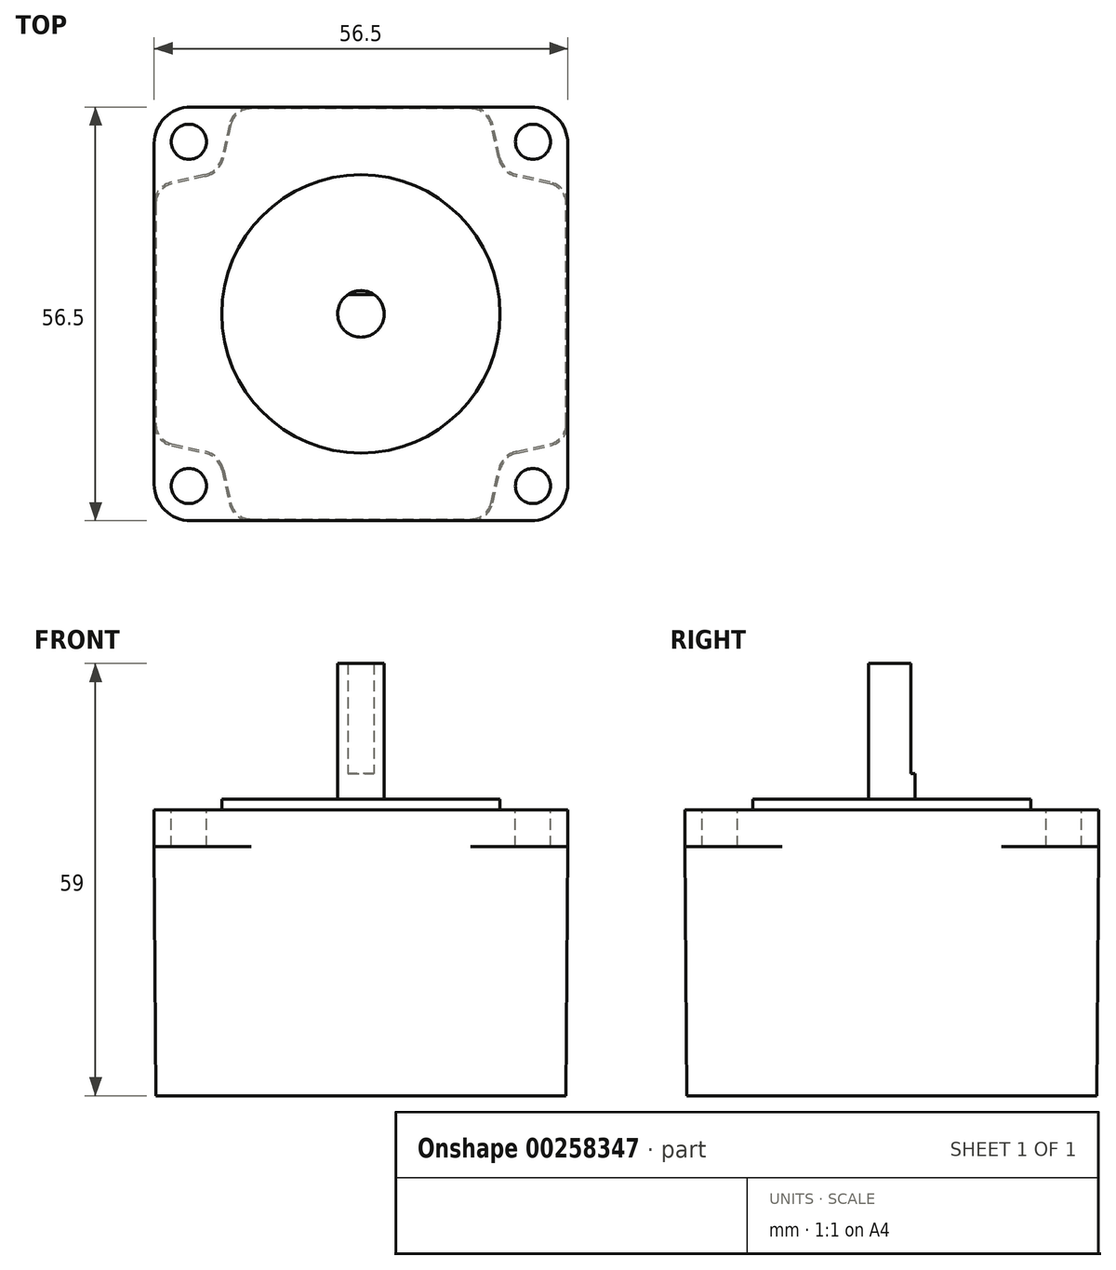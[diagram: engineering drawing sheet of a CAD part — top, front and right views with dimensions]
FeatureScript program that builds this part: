
annotation { "Feature Type Name" : "Feature", "Feature Type Description" : "" }
export const myFeature = defineFeature(function(context is Context, id is Id, definition is map)
    precondition{}
    {
        {
            var Q0;
            Q0=qCreatedBy(makeId("Top.planeOp"),FACE);
            var sketch = newSketch(context, id + "F0", { "sketchPlane" : qUnion([Q0])});
            skLineSegment(sketch, "E0.bottom", {"start": v(28.25, -28.25) * mm, "end": v(-28.25, -28.25) * mm});
            skLineSegment(sketch, "E0.top", {"start": v(28.25, 28.25) * mm, "end": v(-28.25, 28.25) * mm});
            skLineSegment(sketch, "E0.left", {"start": v(28.25, -28.25) * mm, "end": v(28.25, 28.25) * mm});
            skLineSegment(sketch, "E0.right", {"start": v(-28.25, -28.25) * mm, "end": v(-28.25, 28.25) * mm});
            skPoint(sketch, "E0.middle", {"position": v(0, 0) * mm});
            skSolve(sketch);
        }
        {
            var Q0;
            Q0=qSketchRegion(id+"F0",true);
            extrude(context, id + "F1", {"entities" : qUnion([Q0]), "oppositeDirection" : true, "depth" : 5 * mm});
        }
        {
            var Q0;
            Q0=makeQuery(id+"F1.opExtrude","CAP_FACE",FACE,{"disambiguationData":[OSD([sQuery(id+"F0.wireOp",EDGE,"E0.bottom"),sQuery(id+"F0.wireOp",EDGE,"E0.top"),sQuery(id+"F0.wireOp",EDGE,"E0.left"),sQuery(id+"F0.wireOp",EDGE,"E0.right")])],"isStart":false});
            var sketch = newSketch(context, id + "F2", { "sketchPlane" : qUnion([Q0])});
            skLineSegment(sketch, "E1", {"start": v(28.25, 0) * mm, "end": v(-28.25, 0) * mm, "construction": true});
            skLineSegment(sketch, "E2", {"start": v(0, 28.25) * mm, "end": v(0, -28.25) * mm, "construction": true});
            skLineSegment(sketch, "E3", {"start": v(0, 28.25) * mm, "end": v(-15, 28.25) * mm});
            skLineSegment(sketch, "E4", {"start": v(-18, 25.84) * mm, "end": v(-19, 21.33) * mm});
            skLineSegment(sketch, "E5", {"start": v(-21.33, 19) * mm, "end": v(-25.84, 18) * mm});
            skLineSegment(sketch, "E6", {"start": v(-28.25, 15) * mm, "end": v(-28.25, 0) * mm});
            skPoint(sketch, "E7.visualSharp", {"position": v(-19.42, 19.42) * mm});
            skArc(sketch, "E7.filletArc", {"start": v(-21.33, 19) * mm, "mid": v(-19.83, 19.83) * mm, "end": v(-19, 21.33) * mm});
            skPoint(sketch, "E8.visualSharp", {"position": v(-17.47, 28.25) * mm});
            skArc(sketch, "E8.filletArc", {"start": v(-15, 28.25) * mm, "mid": v(-16.92, 27.57) * mm, "end": v(-18, 25.84) * mm});
            skPoint(sketch, "E9.visualSharp", {"position": v(-28.25, 17.47) * mm});
            skArc(sketch, "E9.filletArc", {"start": v(-25.84, 18) * mm, "mid": v(-27.57, 16.92) * mm, "end": v(-28.25, 15) * mm});
            skLineSegment(sketch, "E10.MirrorCS", {"start": v(0, 28.25) * mm, "end": v(15, 28.25) * mm});
            skArc(sketch, "E11.MirrorCS", {"start": v(15, 28.25) * mm, "mid": v(16.92, 27.57) * mm, "end": v(18, 25.84) * mm});
            skLineSegment(sketch, "E12.MirrorCS", {"start": v(18, 25.84) * mm, "end": v(19, 21.33) * mm});
            skArc(sketch, "E13.MirrorCS", {"start": v(21.33, 19) * mm, "mid": v(19.83, 19.83) * mm, "end": v(19, 21.33) * mm});
            skLineSegment(sketch, "E14.MirrorCS", {"start": v(21.33, 19) * mm, "end": v(25.84, 18) * mm});
            skArc(sketch, "E15.MirrorCS", {"start": v(25.84, 18) * mm, "mid": v(27.57, 16.92) * mm, "end": v(28.25, 15) * mm});
            skLineSegment(sketch, "E16.MirrorCS", {"start": v(28.25, 15) * mm, "end": v(28.25, 0) * mm});
            skLineSegment(sketch, "E17.MirrorCS", {"start": v(-28.25, -15) * mm, "end": v(-28.25, 0) * mm});
            skArc(sketch, "E18.MirrorCS", {"start": v(-25.84, -18) * mm, "mid": v(-27.57, -16.92) * mm, "end": v(-28.25, -15) * mm});
            skLineSegment(sketch, "E19.MirrorCS", {"start": v(-21.33, -19) * mm, "end": v(-25.84, -18) * mm});
            skPoint(sketch, "E20.MirrorP", {"position": v(-19.42, -19.42) * mm});
            skArc(sketch, "E21.MirrorCS", {"start": v(-21.33, -19) * mm, "mid": v(-19.83, -19.83) * mm, "end": v(-19, -21.33) * mm});
            skLineSegment(sketch, "E22.MirrorCS", {"start": v(-18, -25.84) * mm, "end": v(-19, -21.33) * mm});
            skArc(sketch, "E23.MirrorCS", {"start": v(-15, -28.25) * mm, "mid": v(-16.92, -27.57) * mm, "end": v(-18, -25.84) * mm});
            skLineSegment(sketch, "E24.MirrorCS", {"start": v(0, -28.25) * mm, "end": v(-15, -28.25) * mm});
            skLineSegment(sketch, "E25.MirrorCS", {"start": v(0, -28.25) * mm, "end": v(15, -28.25) * mm});
            skArc(sketch, "E26.MirrorCS", {"start": v(15, -28.25) * mm, "mid": v(16.92, -27.57) * mm, "end": v(18, -25.84) * mm});
            skLineSegment(sketch, "E27.MirrorCS", {"start": v(18, -25.84) * mm, "end": v(19, -21.33) * mm});
            skArc(sketch, "E28.MirrorCS", {"start": v(21.33, -19) * mm, "mid": v(19.83, -19.83) * mm, "end": v(19, -21.33) * mm});
            skLineSegment(sketch, "E29.MirrorCS", {"start": v(21.33, -19) * mm, "end": v(25.84, -18) * mm});
            skArc(sketch, "E30.MirrorCS", {"start": v(25.84, -18) * mm, "mid": v(27.57, -16.92) * mm, "end": v(28.25, -15) * mm});
            skLineSegment(sketch, "E31.MirrorCS", {"start": v(28.25, -15) * mm, "end": v(28.25, 0) * mm});
            skSolve(sketch);
        }
        {
            var Q0;
            Q0=qSketchRegion(id+"F2",true);
            extrude(context, id + "F3", {"entities" : qUnion([Q0]), "operationType" : NewBodyOperationType.ADD, "depth" : 34 * mm, "hasDraft" : true, "draftAngle" : 0.4 * degree, "draftPullDirection" : true});
        }
        {
            var Q0;
            Q0=makeQuery(id+"F1.opExtrude","CAP_FACE",FACE,{"disambiguationData":[OSD([sQuery(id+"F0.wireOp",EDGE,"E0.bottom"),sQuery(id+"F0.wireOp",EDGE,"E0.top"),sQuery(id+"F0.wireOp",EDGE,"E0.left"),sQuery(id+"F0.wireOp",EDGE,"E0.right")])],"isStart":true});
            var sketch = newSketch(context, id + "F4", { "sketchPlane" : qUnion([Q0])});
            skLineSegment(sketch, "E32", {"start": v(28.25, 0) * mm, "end": v(-28.25, 0) * mm, "construction": true});
            skLineSegment(sketch, "E33", {"start": v(0, 28.25) * mm, "end": v(0, -28.25) * mm, "construction": true});
            skCircle(sketch, "E34", {"center": v(-23.5, 23.5) * mm, "radius": 2.4 * mm});
            skCircle(sketch, "E35.MirrorC", {"center": v(23.5, 23.5) * mm, "radius": 2.4 * mm});
            skCircle(sketch, "E36.MirrorC", {"center": v(-23.5, -23.5) * mm, "radius": 2.4 * mm});
            skCircle(sketch, "E37.MirrorC", {"center": v(23.5, -23.5) * mm, "radius": 2.4 * mm});
            skSolve(sketch);
        }
        {
            var Q0;
            Q0=qSketchRegion(id+"F4",true);
            extrude(context, id + "F5", {"entities" : qUnion([Q0]), "operationType" : NewBodyOperationType.REMOVE, "endBound" : BoundingType.UP_TO_NEXT, "oppositeDirection" : true, "depth" : 25 * mm});
        }
        {
            var Q0;
            Q0=makeQuery(id+"F1.opExtrude","SWEPT_EDGE",EDGE,{"disambiguationData":[OSD([sQuery(id+"F0.wireOp",EDGE,"E0.top"),sQuery(id+"F0.wireOp",EDGE,"E0.left")])]});
            var Q1;
            Q1=makeQuery(id+"F1.opExtrude","SWEPT_EDGE",EDGE,{"disambiguationData":[OSD([sQuery(id+"F0.wireOp",EDGE,"E0.top"),sQuery(id+"F0.wireOp",EDGE,"E0.right")])]});
            var Q2;
            Q2=makeQuery(id+"F1.opExtrude","SWEPT_EDGE",EDGE,{"disambiguationData":[OSD([sQuery(id+"F0.wireOp",EDGE,"E0.bottom"),sQuery(id+"F0.wireOp",EDGE,"E0.right")])]});
            var Q3;
            Q3=makeQuery(id+"F1.opExtrude","SWEPT_EDGE",EDGE,{"disambiguationData":[OSD([sQuery(id+"F0.wireOp",EDGE,"E0.bottom"),sQuery(id+"F0.wireOp",EDGE,"E0.left")])]});
            fillet(context, id + "F6", {"entities" : qUnion([Q0, Q1, Q2, Q3]), "radius" : 5 * mm, "tangentPropagation" : true, "allowEdgeOverflow" : false});
        }
        {
            var Q0;
            Q0=makeQuery(id+"F1.opExtrude","CAP_FACE",FACE,{"disambiguationData":[OSD([sQuery(id+"F0.wireOp",EDGE,"E0.bottom"),sQuery(id+"F0.wireOp",EDGE,"E0.top"),sQuery(id+"F0.wireOp",EDGE,"E0.left"),sQuery(id+"F0.wireOp",EDGE,"E0.right")])],"isStart":true});
            var sketch = newSketch(context, id + "F7", { "sketchPlane" : qUnion([Q0])});
            skCircle(sketch, "E38", {"center": v(0, 0) * mm, "radius": 19 * mm});
            skSolve(sketch);
        }
        {
            var Q0;
            Q0=qSketchRegion(id+"F7",true);
            extrude(context, id + "F8", {"entities" : qUnion([Q0]), "operationType" : NewBodyOperationType.ADD, "depth" : 1.5 * mm});
        }
        {
            var Q0;
            Q0=makeQuery(id+"F8.opExtrude","CAP_FACE",FACE,{"disambiguationData":[OSD([sQuery(id+"F7.wireOp",EDGE,"E38")])],"isStart":false});
            var sketch = newSketch(context, id + "F9", { "sketchPlane" : qUnion([Q0])});
            skCircle(sketch, "E39", {"center": v(0, 0) * mm, "radius": 3.17 * mm});
            skSolve(sketch);
        }
        {
            var Q0;
            Q0=qSketchRegion(id+"F9",true);
            extrude(context, id + "F10", {"entities" : qUnion([Q0]), "operationType" : NewBodyOperationType.ADD, "depth" : 3.5 * mm});
        }
        {
            var Q0;
            Q0=makeQuery(id+"F10.opExtrude","CAP_FACE",FACE,{"disambiguationData":[OSD([sQuery(id+"F9.wireOp",EDGE,"E39")])],"isStart":false});
            var sketch = newSketch(context, id + "F11", { "sketchPlane" : qUnion([Q0])});
            skArc(sketch, "E40.0", {"start": v(-1.79, 2.62) * mm, "mid": v(0, -3.17) * mm, "end": v(1.79, 2.62) * mm});
            skLineSegment(sketch, "E41", {"start": v(-1.79, 2.62) * mm, "end": v(1.79, 2.62) * mm});
            skSolve(sketch);
        }
        {
            var Q0;
            Q0=qSketchRegion(id+"F11",true);
            extrude(context, id + "F12", {"entities" : qUnion([Q0]), "operationType" : NewBodyOperationType.ADD, "depth" : 15 * mm});
        }
    });
